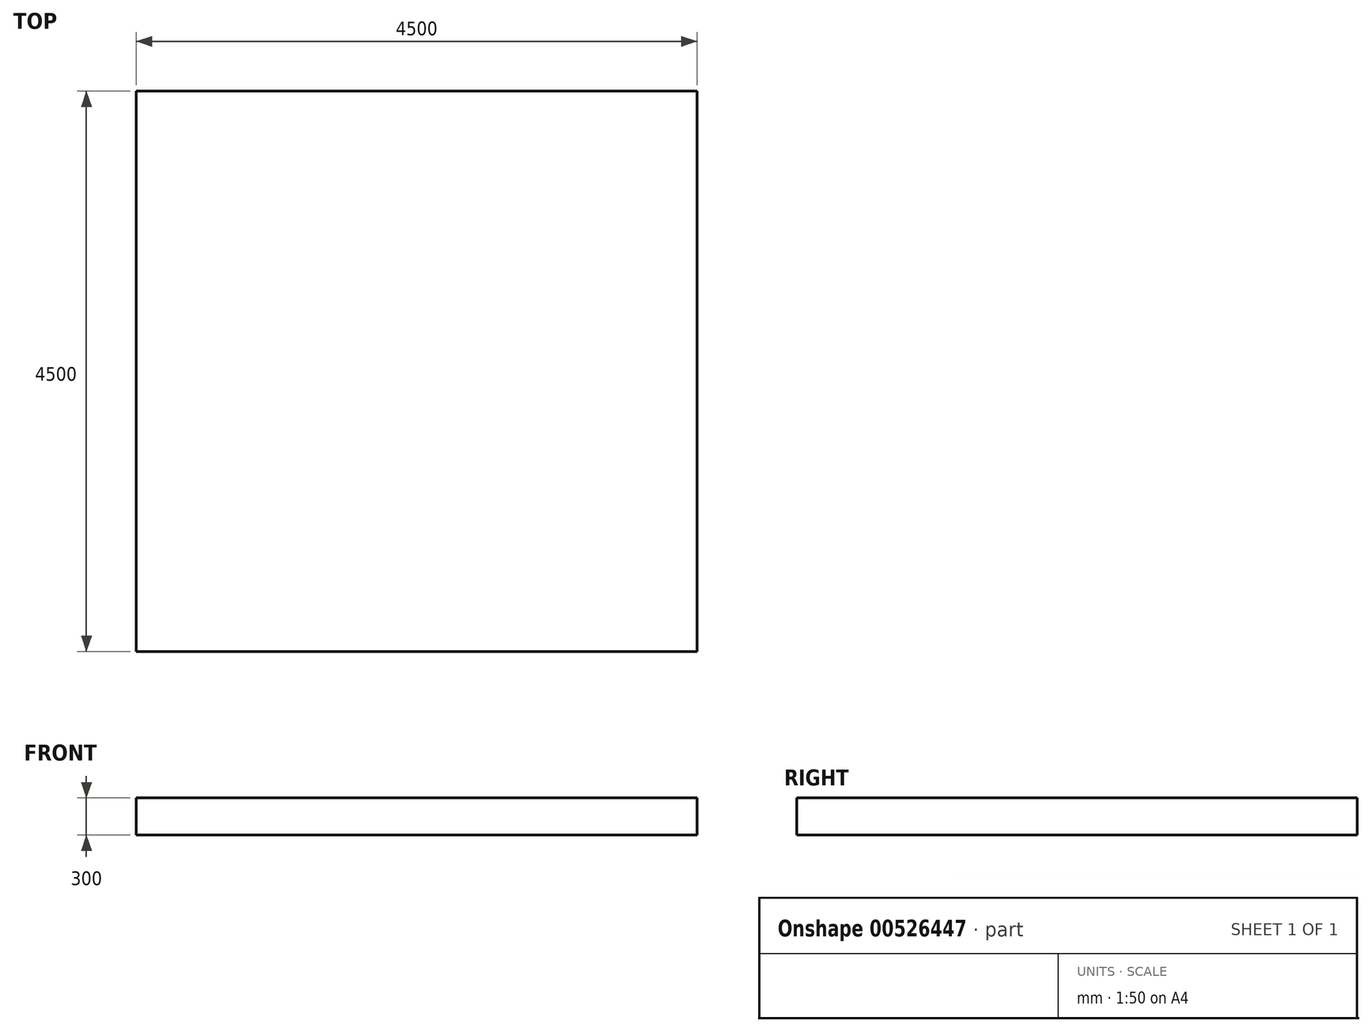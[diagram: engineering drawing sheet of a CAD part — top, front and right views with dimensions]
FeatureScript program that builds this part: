
annotation { "Feature Type Name" : "Feature", "Feature Type Description" : "" }
export const myFeature = defineFeature(function(context is Context, id is Id, definition is map)
    precondition{}
    {
        {
            var Q0;
            Q0=qCreatedBy(makeId("Top.planeOp"),FACE);
            var sketch = newSketch(context, id + "F0", { "sketchPlane" : qUnion([Q0])});
            skLineSegment(sketch, "E0.bottom", {"start": v(2250, 2250) * mm, "end": v(-2250, 2250) * mm});
            skLineSegment(sketch, "E0.top", {"start": v(2250, -2250) * mm, "end": v(-2250, -2250) * mm});
            skLineSegment(sketch, "E0.left", {"start": v(2250, 2250) * mm, "end": v(2250, -2250) * mm});
            skLineSegment(sketch, "E0.right", {"start": v(-2250, 2250) * mm, "end": v(-2250, -2250) * mm});
            skPoint(sketch, "E0.middle", {"position": v(0, 0) * mm});
            skSolve(sketch);
        }
        {
            var Q0;
            Q0=makeQuery(id+"F0.imprint","IMPRINT",FACE,{"disambiguationData":[TD([[makeQuery(id+"F0.imprint","IMPRINT",EDGE,{"derivedFrom":sQuery(id+"F0.wireOp",EDGE,"E0.bottom")}),1.0]])]});
            extrude(context, id + "F1", {"entities" : qUnion([Q0]), "oppositeDirection" : true, "depth" : 300 * mm, "offsetDistance" : 25 * mm});
        }
    });
